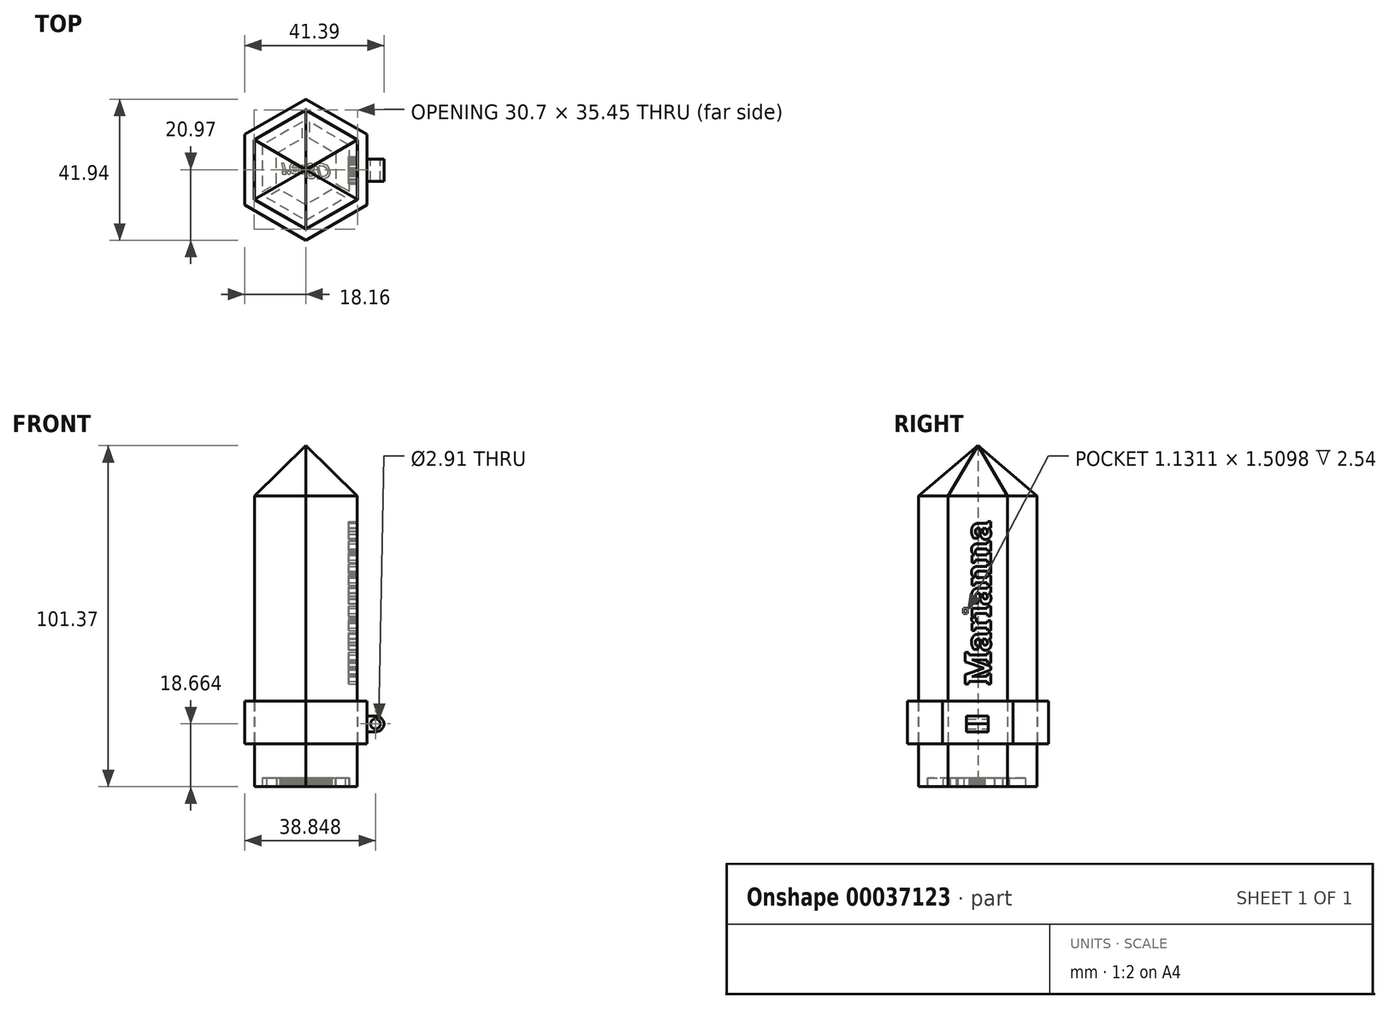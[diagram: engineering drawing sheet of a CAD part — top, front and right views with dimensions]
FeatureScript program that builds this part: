
annotation { "Feature Type Name" : "Feature", "Feature Type Description" : "" }
export const myFeature = defineFeature(function(context is Context, id is Id, definition is map)
    precondition{}
    {
        {
            var Q0;
            Q0=qCreatedBy(makeId("Top.planeOp"),FACE);
            var sketch = newSketch(context, id + "F0", { "sketchPlane" : qUnion([Q0])});
            skCircle(sketch, "E0.cCircle", {"center": v(0, 0) * mm, "radius": 15.24 * mm, "construction": true});
            skLineSegment(sketch, "E0.0", {"start": v(15.24, 8.8) * mm, "end": v(15.24, -8.8) * mm});
            skLineSegment(sketch, "E0.1", {"start": v(15.24, -8.8) * mm, "end": v(0, -17.6) * mm});
            skLineSegment(sketch, "E0.2", {"start": v(0, -17.6) * mm, "end": v(-15.24, -8.8) * mm});
            skLineSegment(sketch, "E0.3", {"start": v(-15.24, -8.8) * mm, "end": v(-15.24, 8.8) * mm});
            skLineSegment(sketch, "E0.4", {"start": v(-15.24, 8.8) * mm, "end": v(0, 17.6) * mm});
            skLineSegment(sketch, "E0.5", {"start": v(0, 17.6) * mm, "end": v(15.24, 8.8) * mm});
            skPoint(sketch, "E0.0.midPoint", {"position": v(15.24, 0) * mm});
            skLineSegment(sketch, "E1", {"start": v(0, 17.6) * mm, "end": v(0, -17.6) * mm});
            skLineSegment(sketch, "E2", {"start": v(-15.24, 8.8) * mm, "end": v(15.24, -8.8) * mm});
            skLineSegment(sketch, "E3", {"start": v(15.24, 8.8) * mm, "end": v(-15.24, -8.8) * mm});
            skSolve(sketch);
        }
        {
            var Q0;
            {var subQ3=sQuery(id+"F0.wireOp",EDGE,"E0.0");Q0=makeQuery(id+"F0.imprint","IMPRINT",FACE,{"disambiguationData":[TD([[makeQuery(id+"F0.imprint","IMPRINT",EDGE,{"derivedFrom":subQ3}),-1.0]])]});}
            extrude(context, id + "F1", {"entities" : qUnion([Q0]), "depth" : 101.6 * mm});
        }
        {
            var Q0;
            Q0=qCreatedBy(makeId("Front.planeOp"),FACE);
            var sketch = newSketch(context, id + "F2", { "sketchPlane" : qUnion([Q0])});
            skLineSegment(sketch, "E4", {"start": v(0, 101.37) * mm, "end": v(19.32, 82.36) * mm});
            skLineSegment(sketch, "E5", {"start": v(19.32, 82.36) * mm, "end": v(19.32, 105.1) * mm});
            skLineSegment(sketch, "E6", {"start": v(19.32, 105.1) * mm, "end": v(0, 105.1) * mm});
            skLineSegment(sketch, "E7", {"start": v(0, 105.1) * mm, "end": v(0, 101.37) * mm});
            skSolve(sketch);
        }
        {
            var Q0;
            Q0 = qSketchRegion(id + "F2", true);
            extrude(context, id + "F3", {"entities" : qUnion([Q0]), "operationType" : NewBodyOperationType.REMOVE, "endBound" : BoundingType.SYMMETRIC, "oppositeDirection" : true, "depth" : 50.8 * mm});
        }
        {
            var Q0;
            Q0=makeQuery(id+"F1.opExtrude","SWEPT_BODY",BODY,{"disambiguationData":[OSD([sQuery(id+"F0.wireOp",EDGE,"E0.0"),sQuery(id+"F0.wireOp",EDGE,"E2"),sQuery(id+"F0.wireOp",EDGE,"E3")])]});
            var Q1;
            Q1=makeQuery(id+"F1.opExtrude","SWEPT_EDGE",EDGE,{"disambiguationData":[OSD([sQuery(id+"F0.wireOp",EDGE,"E1"),sQuery(id+"F0.wireOp",EDGE,"E2"),sQuery(id+"F0.wireOp",EDGE,"E3")])]});
            circularPattern(context, id + "F4", {"entities" : qUnion([Q0]), "axis" : qUnion([Q1]), "angle" : 60 * degree, "instanceCount" : 6});
        }
        {
            var Q0;
            Q0=qCreatedBy(makeId("Top.planeOp"),FACE);
            var sketch = newSketch(context, id + "F5", { "sketchPlane" : qUnion([Q0])});
            skCircle(sketch, "E8.cCircle", {"center": v(0, 0) * mm, "radius": 18.16 * mm, "construction": true});
            skLineSegment(sketch, "E8.0", {"start": v(18.16, 10.49) * mm, "end": v(18.16, -10.49) * mm});
            skLineSegment(sketch, "E8.1", {"start": v(18.16, -10.49) * mm, "end": v(0, -20.97) * mm});
            skLineSegment(sketch, "E8.2", {"start": v(0, -20.97) * mm, "end": v(-18.16, -10.49) * mm});
            skLineSegment(sketch, "E8.3", {"start": v(-18.16, -10.49) * mm, "end": v(-18.16, 10.49) * mm});
            skLineSegment(sketch, "E8.4", {"start": v(-18.16, 10.49) * mm, "end": v(0, 20.97) * mm});
            skLineSegment(sketch, "E8.5", {"start": v(0, 20.97) * mm, "end": v(18.16, 10.49) * mm});
            skPoint(sketch, "E8.0.midPoint", {"position": v(18.16, 0) * mm});
            skCircle(sketch, "E9.cCircle", {"center": v(0, 0) * mm, "radius": 15.35 * mm, "construction": true});
            skLineSegment(sketch, "E9.0", {"start": v(15.35, 8.86) * mm, "end": v(15.35, -8.86) * mm});
            skLineSegment(sketch, "E9.1", {"start": v(15.35, -8.86) * mm, "end": v(0, -17.73) * mm});
            skLineSegment(sketch, "E9.2", {"start": v(0, -17.73) * mm, "end": v(-15.35, -8.86) * mm});
            skLineSegment(sketch, "E9.3", {"start": v(-15.35, -8.86) * mm, "end": v(-15.35, 8.86) * mm});
            skLineSegment(sketch, "E9.4", {"start": v(-15.35, 8.86) * mm, "end": v(0, 17.73) * mm});
            skLineSegment(sketch, "E9.5", {"start": v(0, 17.73) * mm, "end": v(15.35, 8.86) * mm});
            skPoint(sketch, "E9.0.midPoint", {"position": v(15.35, 0) * mm});
            skSolve(sketch);
        }
        {
            var Q0;
            Q0 = qSketchRegion(id + "F5", true);
            extrude(context, id + "F6", {"entities" : qUnion([Q0]), "depth" : 25.4 * mm});
        }
        {
            var Q0;
            Q0 = qSketchRegion(id + "F5", true);
            extrude(context, id + "F7", {"entities" : qUnion([Q0]), "operationType" : NewBodyOperationType.REMOVE, "depth" : 12.7 * mm});
        }
        {
            var Q0;
            Q0=makeQuery(id+"F6.opExtrude","SWEPT_FACE",FACE,{"disambiguationData":[OSD([sQuery(id+"F5.wireOp",EDGE,"E8.0")])]});
            var sketch = newSketch(context, id + "F8", { "sketchPlane" : qUnion([Q0])});
            skPoint(sketch, "E10.firstSnap0", {"position": v(-10.49, 19.05) * mm});
            skLineSegment(sketch, "E11.bottom", {"start": v(-3.45, 20.98) * mm, "end": v(3.13, 20.98) * mm});
            skLineSegment(sketch, "E11.top", {"start": v(-3.45, 16.34) * mm, "end": v(3.13, 16.34) * mm});
            skLineSegment(sketch, "E11.left", {"start": v(-3.45, 20.98) * mm, "end": v(-3.45, 16.34) * mm});
            skLineSegment(sketch, "E11.right", {"start": v(3.13, 20.98) * mm, "end": v(3.13, 16.34) * mm});
            skSolve(sketch);
        }
        {
            var Q0;
            Q0=makeQuery(id+"F8.imprint","IMPRINT",FACE,{"disambiguationData":[TD([[makeQuery(id+"F8.imprint","IMPRINT",EDGE,{"derivedFrom":sQuery(id+"F8.wireOp",EDGE,"E11.bottom")}),-1.0]])]});
            extrude(context, id + "F9", {"entities" : qUnion([Q0]), "operationType" : NewBodyOperationType.ADD, "depth" : 5.08 * mm});
        }
        {
            var Q0;
            Q0=makeQuery(id+"F9.opExtrude","SWEPT_FACE",FACE,{"disambiguationData":[OSD([sQuery(id+"F8.wireOp",EDGE,"E11.right")])]});
            var sketch = newSketch(context, id + "F10", { "sketchPlane" : qUnion([Q0])});
            skCircle(sketch, "E12", {"center": v(-20.69, 18.66) * mm, "radius": 1.46 * mm});
            skSolve(sketch);
        }
        {
            var Q0;
            Q0 = qSketchRegion(id + "F10", true);
            extrude(context, id + "F11", {"entities" : qUnion([Q0]), "operationType" : NewBodyOperationType.REMOVE, "endBound" : BoundingType.SYMMETRIC, "oppositeDirection" : true, "depth" : 25.4 * mm});
        }
        {
            var Q0;
            Q0=makeQuery(id+"F9.opExtrude","CAP_EDGE",EDGE,{"disambiguationData":[OSD([sQuery(id+"F8.wireOp",EDGE,"E11.bottom")])],"isStart":false});
            var Q1;
            Q1=makeQuery(id+"F9.opExtrude","CAP_EDGE",EDGE,{"disambiguationData":[OSD([sQuery(id+"F8.wireOp",EDGE,"E11.top")])],"isStart":false});
            fillet(context, id + "F12", {"entities" : qUnion([Q0, Q1]), "radius" : 2.54 * mm, "tangentPropagation" : true, "allowEdgeOverflow" : false});
        }
        {
            var Q0;
            Q0=makeQuery(id+"F4.opPattern","COPY",EDGE,{"derivedFrom":makeQuery(id+"F1.opExtrude","CAP_EDGE",EDGE,{"disambiguationData":[OSD([sQuery(id+"F0.wireOp",EDGE,"E0.0")])],"isStart":true}),"instanceName":"3"});
            cPlane(context, id + "F13", {"entities" : qUnion([Q0]), "cplaneType" : CPlaneType.LINE_ANGLE, "offset" : 152.4 * mm, "angle" : 180 * degree, "width" : 152.4 * mm, "height" : 152.4 * mm});
        }
        {
            var Q0;
            Q0=qCreatedBy(id+"F13.planeOp",FACE);
            var sketch = newSketch(context, id + "F14", { "sketchPlane" : qUnion([Q0])});
            skLineSegment(sketch, "E13", {"start": v(6.15, 1.61) * mm, "end": v(5.9, 1.8) * mm});
            skLineSegment(sketch, "E14", {"start": v(5.9, 1.8) * mm, "end": v(5.6, 1.94) * mm});
            skLineSegment(sketch, "E15", {"start": v(5.6, 1.94) * mm, "end": v(5.26, 2.03) * mm});
            skLineSegment(sketch, "E16", {"start": v(5.26, 2.03) * mm, "end": v(4.85, 2.05) * mm});
            skLineSegment(sketch, "E17", {"start": v(4.85, 2.05) * mm, "end": v(4.55, 2.05) * mm});
            skLineSegment(sketch, "E18", {"start": v(4.55, 2.05) * mm, "end": v(3.77, -1.27) * mm});
            skLineSegment(sketch, "E19", {"start": v(3.77, -1.27) * mm, "end": v(4.36, -1.27) * mm});
            skLineSegment(sketch, "E20", {"start": v(4.36, -1.27) * mm, "end": v(5.29, -1.13) * mm});
            skLineSegment(sketch, "E21", {"start": v(5.29, -1.13) * mm, "end": v(6, -0.67) * mm});
            skLineSegment(sketch, "E22", {"start": v(6, -0.67) * mm, "end": v(6.22, -0.39) * mm});
            skLineSegment(sketch, "E23", {"start": v(6.22, -0.39) * mm, "end": v(6.39, -0.07) * mm});
            skLineSegment(sketch, "E24", {"start": v(6.39, -0.07) * mm, "end": v(6.49, 0.28) * mm});
            skLineSegment(sketch, "E25", {"start": v(6.49, 0.28) * mm, "end": v(6.52, 0.65) * mm});
            skLineSegment(sketch, "E26", {"start": v(6.52, 0.65) * mm, "end": v(6.43, 1.18) * mm});
            skLineSegment(sketch, "E27", {"start": v(6.43, 1.18) * mm, "end": v(6.15, 1.61) * mm});
            skLineSegment(sketch, "E28", {"start": v(-2.68, 0.11) * mm, "end": v(-2.71, 0.3) * mm});
            skLineSegment(sketch, "E29", {"start": v(-2.71, 0.3) * mm, "end": v(-2.82, 0.45) * mm});
            skLineSegment(sketch, "E30", {"start": v(-2.82, 0.45) * mm, "end": v(-3, 0.55) * mm});
            skLineSegment(sketch, "E31", {"start": v(-3, 0.55) * mm, "end": v(-3.23, 0.58) * mm});
            skLineSegment(sketch, "E32", {"start": v(-3.23, 0.58) * mm, "end": v(-3.5, 0.53) * mm});
            skLineSegment(sketch, "E33", {"start": v(-3.5, 0.53) * mm, "end": v(-3.72, 0.4) * mm});
            skLineSegment(sketch, "E34", {"start": v(-3.72, 0.4) * mm, "end": v(-3.9, 0.18) * mm});
            skLineSegment(sketch, "E35", {"start": v(-3.9, 0.18) * mm, "end": v(-4.04, -0.1) * mm});
            skLineSegment(sketch, "E36", {"start": v(-4.04, -0.1) * mm, "end": v(-2.7, -0.1) * mm});
            skLineSegment(sketch, "E37", {"start": v(-2.7, -0.1) * mm, "end": v(-2.68, 0.11) * mm});
            skLineSegment(sketch, "E38", {"start": v(0, 17.6) * mm, "end": v(-15.24, 8.8) * mm});
            skLineSegment(sketch, "E39", {"start": v(-15.24, 8.8) * mm, "end": v(-15.24, -8.8) * mm});
            skLineSegment(sketch, "E40", {"start": v(-15.24, -8.8) * mm, "end": v(0, -17.6) * mm});
            skLineSegment(sketch, "E41", {"start": v(0, -17.6) * mm, "end": v(15.24, -8.8) * mm});
            skLineSegment(sketch, "E42", {"start": v(15.24, -8.8) * mm, "end": v(15.24, 8.8) * mm});
            skLineSegment(sketch, "E43", {"start": v(15.24, 8.8) * mm, "end": v(0, 17.6) * mm});
            skLineSegment(sketch, "E44", {"start": v(0, 15) * mm, "end": v(11.75, 8.22) * mm});
            skLineSegment(sketch, "E45", {"start": v(11.75, 8.22) * mm, "end": v(7.78, 5.93) * mm});
            skLineSegment(sketch, "E46", {"start": v(7.78, 5.93) * mm, "end": v(0.02, 10.41) * mm});
            skLineSegment(sketch, "E47", {"start": v(0.02, 10.41) * mm, "end": v(-7.75, 5.93) * mm});
            skLineSegment(sketch, "E48", {"start": v(-7.75, 5.93) * mm, "end": v(-11.73, 8.23) * mm});
            skLineSegment(sketch, "E49", {"start": v(-11.73, 8.23) * mm, "end": v(0, 15) * mm});
            skLineSegment(sketch, "E50", {"start": v(3.31, 1.95) * mm, "end": v(3.47, 2.64) * mm});
            skLineSegment(sketch, "E51", {"start": v(3.47, 2.64) * mm, "end": v(4.94, 2.64) * mm});
            skLineSegment(sketch, "E52", {"start": v(4.94, 2.64) * mm, "end": v(6, 2.46) * mm});
            skLineSegment(sketch, "E53", {"start": v(6, 2.46) * mm, "end": v(6.71, 2) * mm});
            skLineSegment(sketch, "E54", {"start": v(6.71, 2) * mm, "end": v(6.93, 1.73) * mm});
            skLineSegment(sketch, "E55", {"start": v(6.93, 1.73) * mm, "end": v(7.1, 1.4) * mm});
            skLineSegment(sketch, "E56", {"start": v(7.1, 1.4) * mm, "end": v(7.18, 1.05) * mm});
            skLineSegment(sketch, "E57", {"start": v(7.18, 1.05) * mm, "end": v(7.22, 0.68) * mm});
            skLineSegment(sketch, "E58", {"start": v(7.22, 0.68) * mm, "end": v(7.04, -0.28) * mm});
            skLineSegment(sketch, "E59", {"start": v(7.04, -0.28) * mm, "end": v(6.5, -1.05) * mm});
            skLineSegment(sketch, "E60", {"start": v(6.5, -1.05) * mm, "end": v(6.04, -1.42) * mm});
            skLineSegment(sketch, "E61", {"start": v(6.04, -1.42) * mm, "end": v(5.5, -1.66) * mm});
            skLineSegment(sketch, "E62", {"start": v(5.5, -1.66) * mm, "end": v(4.9, -1.8) * mm});
            skLineSegment(sketch, "E63", {"start": v(4.9, -1.8) * mm, "end": v(4.25, -1.85) * mm});
            skLineSegment(sketch, "E64", {"start": v(4.25, -1.85) * mm, "end": v(2.5, -1.85) * mm});
            skLineSegment(sketch, "E65", {"start": v(2.5, -1.85) * mm, "end": v(2.66, -1.16) * mm});
            skLineSegment(sketch, "E66", {"start": v(2.66, -1.16) * mm, "end": v(3.13, -1.16) * mm});
            skLineSegment(sketch, "E67", {"start": v(3.13, -1.16) * mm, "end": v(3.86, 1.95) * mm});
            skLineSegment(sketch, "E68", {"start": v(3.86, 1.95) * mm, "end": v(3.31, 1.95) * mm});
            skLineSegment(sketch, "E69", {"start": v(-7.17, 0.62) * mm, "end": v(-7, 1.25) * mm});
            skLineSegment(sketch, "E70", {"start": v(-7, 1.25) * mm, "end": v(-5.84, 1.25) * mm});
            skLineSegment(sketch, "E71", {"start": v(-5.84, 1.25) * mm, "end": v(-6.03, 0.37) * mm});
            skLineSegment(sketch, "E72", {"start": v(-6.03, 0.37) * mm, "end": v(-5.77, 0.79) * mm});
            skLineSegment(sketch, "E73", {"start": v(-5.77, 0.79) * mm, "end": v(-5.5, 1.08) * mm});
            skLineSegment(sketch, "E74", {"start": v(-5.5, 1.08) * mm, "end": v(-5.24, 1.25) * mm});
            skLineSegment(sketch, "E75", {"start": v(-5.24, 1.25) * mm, "end": v(-4.97, 1.3) * mm});
            skLineSegment(sketch, "E76", {"start": v(-4.97, 1.3) * mm, "end": v(-4.79, 1.27) * mm});
            skLineSegment(sketch, "E77", {"start": v(-4.79, 1.27) * mm, "end": v(-4.63, 1.17) * mm});
            skLineSegment(sketch, "E78", {"start": v(-4.63, 1.17) * mm, "end": v(-4.52, 1.01) * mm});
            skLineSegment(sketch, "E79", {"start": v(-4.52, 1.01) * mm, "end": v(-4.47, 0.81) * mm});
            skLineSegment(sketch, "E80", {"start": v(-4.47, 0.81) * mm, "end": v(-4.5, 0.63) * mm});
            skLineSegment(sketch, "E81", {"start": v(-4.5, 0.63) * mm, "end": v(-4.61, 0.48) * mm});
            skLineSegment(sketch, "E82", {"start": v(-4.61, 0.48) * mm, "end": v(-4.76, 0.38) * mm});
            skLineSegment(sketch, "E83", {"start": v(-4.76, 0.38) * mm, "end": v(-4.94, 0.34) * mm});
            skLineSegment(sketch, "E84", {"start": v(-4.94, 0.34) * mm, "end": v(-5.11, 0.37) * mm});
            skLineSegment(sketch, "E85", {"start": v(-5.11, 0.37) * mm, "end": v(-5.25, 0.45) * mm});
            skLineSegment(sketch, "E86", {"start": v(-5.25, 0.45) * mm, "end": v(-5.34, 0.56) * mm});
            skLineSegment(sketch, "E87", {"start": v(-5.34, 0.56) * mm, "end": v(-5.4, 0.68) * mm});
            skLineSegment(sketch, "E88", {"start": v(-5.4, 0.68) * mm, "end": v(-5.58, 0.57) * mm});
            skLineSegment(sketch, "E89", {"start": v(-5.58, 0.57) * mm, "end": v(-5.78, 0.35) * mm});
            skLineSegment(sketch, "E90", {"start": v(-5.78, 0.35) * mm, "end": v(-5.97, 0.03) * mm});
            skLineSegment(sketch, "E91", {"start": v(-5.97, 0.03) * mm, "end": v(-6.11, -0.38) * mm});
            skLineSegment(sketch, "E92", {"start": v(-6.11, -0.38) * mm, "end": v(-6.45, -1.89) * mm});
            skLineSegment(sketch, "E93", {"start": v(-6.45, -1.89) * mm, "end": v(-7.22, -1.89) * mm});
            skLineSegment(sketch, "E94", {"start": v(-7.22, -1.89) * mm, "end": v(-6.62, 0.62) * mm});
            skLineSegment(sketch, "E95", {"start": v(-6.62, 0.62) * mm, "end": v(-7.17, 0.62) * mm});
            skLineSegment(sketch, "E96", {"start": v(-7.17, 0.62) * mm, "end": v(-7.17, 0.62) * mm});
            skLineSegment(sketch, "E97", {"start": v(-1.06, -14.18) * mm, "end": v(-12.9, -7.34) * mm});
            skLineSegment(sketch, "E98", {"start": v(-12.9, -7.34) * mm, "end": v(-12.9, 6.46) * mm});
            skLineSegment(sketch, "E99", {"start": v(-12.9, 6.46) * mm, "end": v(-8.8, 4.1) * mm});
            skLineSegment(sketch, "E100", {"start": v(-8.8, 4.1) * mm, "end": v(-8.8, -4.87) * mm});
            skLineSegment(sketch, "E101", {"start": v(-8.8, -4.87) * mm, "end": v(-1.06, -9.34) * mm});
            skLineSegment(sketch, "E102", {"start": v(-1.06, -9.34) * mm, "end": v(-1.06, -14.18) * mm});
            skLineSegment(sketch, "E103", {"start": v(-1.02, -1.29) * mm, "end": v(-1.25, -1.24) * mm});
            skLineSegment(sketch, "E104", {"start": v(-1.25, -1.24) * mm, "end": v(-1.42, -1.1) * mm});
            skLineSegment(sketch, "E105", {"start": v(-1.42, -1.1) * mm, "end": v(-1.8, -1.28) * mm});
            skLineSegment(sketch, "E106", {"start": v(-1.8, -1.28) * mm, "end": v(-2.2, -1.6) * mm});
            skLineSegment(sketch, "E107", {"start": v(-2.2, -1.6) * mm, "end": v(-2.73, -1.89) * mm});
            skLineSegment(sketch, "E108", {"start": v(-2.73, -1.89) * mm, "end": v(-3.48, -2.02) * mm});
            skLineSegment(sketch, "E109", {"start": v(-3.48, -2.02) * mm, "end": v(-3.7, -2) * mm});
            skLineSegment(sketch, "E110", {"start": v(-3.7, -2) * mm, "end": v(-3.93, -1.92) * mm});
            skLineSegment(sketch, "E111", {"start": v(-3.93, -1.92) * mm, "end": v(-4.17, -1.8) * mm});
            skLineSegment(sketch, "E112", {"start": v(-4.17, -1.8) * mm, "end": v(-4.38, -1.63) * mm});
            skLineSegment(sketch, "E113", {"start": v(-4.38, -1.63) * mm, "end": v(-4.57, -1.43) * mm});
            skLineSegment(sketch, "E114", {"start": v(-4.57, -1.43) * mm, "end": v(-4.73, -1.2) * mm});
            skLineSegment(sketch, "E115", {"start": v(-4.73, -1.2) * mm, "end": v(-4.82, -0.92) * mm});
            skLineSegment(sketch, "E116", {"start": v(-4.82, -0.92) * mm, "end": v(-4.86, -0.62) * mm});
            skLineSegment(sketch, "E117", {"start": v(-4.86, -0.62) * mm, "end": v(-4.73, 0.09) * mm});
            skLineSegment(sketch, "E118", {"start": v(-4.73, 0.09) * mm, "end": v(-4.39, 0.66) * mm});
            skLineSegment(sketch, "E119", {"start": v(-4.39, 0.66) * mm, "end": v(-3.87, 1.05) * mm});
            skLineSegment(sketch, "E120", {"start": v(-3.87, 1.05) * mm, "end": v(-3.24, 1.2) * mm});
            skLineSegment(sketch, "E121", {"start": v(-3.24, 1.2) * mm, "end": v(-2.72, 1.12) * mm});
            skLineSegment(sketch, "E122", {"start": v(-2.72, 1.12) * mm, "end": v(-2.32, 0.9) * mm});
            skLineSegment(sketch, "E123", {"start": v(-2.32, 0.9) * mm, "end": v(-2.05, 0.53) * mm});
            skLineSegment(sketch, "E124", {"start": v(-2.05, 0.53) * mm, "end": v(-1.96, 0.04) * mm});
            skLineSegment(sketch, "E125", {"start": v(-1.96, 0.04) * mm, "end": v(-1.99, -0.27) * mm});
            skLineSegment(sketch, "E126", {"start": v(-1.99, -0.27) * mm, "end": v(-2.07, -0.61) * mm});
            skLineSegment(sketch, "E127", {"start": v(-2.07, -0.61) * mm, "end": v(-4.12, -0.61) * mm});
            skLineSegment(sketch, "E128", {"start": v(-4.12, -0.61) * mm, "end": v(-4.12, -0.66) * mm});
            skLineSegment(sketch, "E129", {"start": v(-4.12, -0.66) * mm, "end": v(-4.07, -0.91) * mm});
            skLineSegment(sketch, "E130", {"start": v(-4.07, -0.91) * mm, "end": v(-3.9, -1.15) * mm});
            skLineSegment(sketch, "E131", {"start": v(-3.9, -1.15) * mm, "end": v(-3.63, -1.32) * mm});
            skLineSegment(sketch, "E132", {"start": v(-3.63, -1.32) * mm, "end": v(-3.26, -1.4) * mm});
            skLineSegment(sketch, "E133", {"start": v(-3.26, -1.4) * mm, "end": v(-2.72, -1.29) * mm});
            skLineSegment(sketch, "E134", {"start": v(-2.72, -1.29) * mm, "end": v(-2.2, -1.01) * mm});
            skLineSegment(sketch, "E135", {"start": v(-2.2, -1.01) * mm, "end": v(-1.76, -0.68) * mm});
            skLineSegment(sketch, "E136", {"start": v(-1.76, -0.68) * mm, "end": v(-1.43, -0.4) * mm});
            skLineSegment(sketch, "E137", {"start": v(-1.43, -0.4) * mm, "end": v(-1.3, -0.3) * mm});
            skLineSegment(sketch, "E138", {"start": v(-1.3, -0.3) * mm, "end": v(-1.24, -0.28) * mm});
            skLineSegment(sketch, "E139", {"start": v(-1.24, -0.28) * mm, "end": v(-1.22, -0.28) * mm});
            skLineSegment(sketch, "E140", {"start": v(-1.22, -0.28) * mm, "end": v(-1.02, -0.24) * mm});
            skLineSegment(sketch, "E141", {"start": v(-1.02, -0.24) * mm, "end": v(-0.82, -0.28) * mm});
            skLineSegment(sketch, "E142", {"start": v(-0.82, -0.28) * mm, "end": v(-0.65, -0.4) * mm});
            skLineSegment(sketch, "E143", {"start": v(-0.65, -0.4) * mm, "end": v(-0.54, -0.56) * mm});
            skLineSegment(sketch, "E144", {"start": v(-0.54, -0.56) * mm, "end": v(-0.5, -0.76) * mm});
            skLineSegment(sketch, "E145", {"start": v(-0.5, -0.76) * mm, "end": v(-0.54, -0.97) * mm});
            skLineSegment(sketch, "E146", {"start": v(-0.54, -0.97) * mm, "end": v(-0.65, -1.13) * mm});
            skLineSegment(sketch, "E147", {"start": v(-0.65, -1.13) * mm, "end": v(-0.82, -1.25) * mm});
            skLineSegment(sketch, "E148", {"start": v(-0.82, -1.25) * mm, "end": v(-1.02, -1.29) * mm});
            skLineSegment(sketch, "E149", {"start": v(-0.67, 0.24) * mm, "end": v(-0.7, 0.22) * mm});
            skLineSegment(sketch, "E150", {"start": v(-0.7, 0.22) * mm, "end": v(-0.77, 0.19) * mm});
            skLineSegment(sketch, "E151", {"start": v(-0.77, 0.19) * mm, "end": v(-1.01, 0.13) * mm});
            skLineSegment(sketch, "E152", {"start": v(-1.01, 0.13) * mm, "end": v(-1.22, 0.17) * mm});
            skLineSegment(sketch, "E153", {"start": v(-1.22, 0.17) * mm, "end": v(-1.4, 0.29) * mm});
            skLineSegment(sketch, "E154", {"start": v(-1.4, 0.29) * mm, "end": v(-1.51, 0.46) * mm});
            skLineSegment(sketch, "E155", {"start": v(-1.51, 0.46) * mm, "end": v(-1.55, 0.67) * mm});
            skLineSegment(sketch, "E156", {"start": v(-1.55, 0.67) * mm, "end": v(-1.51, 0.88) * mm});
            skLineSegment(sketch, "E157", {"start": v(-1.51, 0.88) * mm, "end": v(-1.4, 1.05) * mm});
            skLineSegment(sketch, "E158", {"start": v(-1.4, 1.05) * mm, "end": v(-1.23, 1.17) * mm});
            skLineSegment(sketch, "E159", {"start": v(-1.23, 1.17) * mm, "end": v(-1.02, 1.2) * mm});
            skLineSegment(sketch, "E160", {"start": v(-1.02, 1.2) * mm, "end": v(-1.01, 1.21) * mm});
            skLineSegment(sketch, "E161", {"start": v(-1.01, 1.21) * mm, "end": v(-1, 1.21) * mm});
            skLineSegment(sketch, "E162", {"start": v(-1, 1.21) * mm, "end": v(-0.97, 1.2) * mm});
            skLineSegment(sketch, "E163", {"start": v(-0.97, 1.2) * mm, "end": v(-0.96, 1.2) * mm});
            skLineSegment(sketch, "E164", {"start": v(-0.96, 1.2) * mm, "end": v(-0.95, 1.2) * mm});
            skLineSegment(sketch, "E165", {"start": v(-0.95, 1.2) * mm, "end": v(-0.94, 1.2) * mm});
            skLineSegment(sketch, "E166", {"start": v(-0.94, 1.2) * mm, "end": v(-0.78, 1.16) * mm});
            skLineSegment(sketch, "E167", {"start": v(-0.78, 1.16) * mm, "end": v(-0.46, 0.95) * mm});
            skLineSegment(sketch, "E168", {"start": v(-0.46, 0.95) * mm, "end": v(-0.2, 0.62) * mm});
            skLineSegment(sketch, "E169", {"start": v(-0.2, 0.62) * mm, "end": v(0.02, 0.21) * mm});
            skLineSegment(sketch, "E170", {"start": v(0.02, 0.21) * mm, "end": v(0.22, -0.21) * mm});
            skLineSegment(sketch, "E171", {"start": v(0.22, -0.21) * mm, "end": v(0.41, -0.62) * mm});
            skLineSegment(sketch, "E172", {"start": v(0.41, -0.62) * mm, "end": v(0.63, -0.96) * mm});
            skLineSegment(sketch, "E173", {"start": v(0.63, -0.96) * mm, "end": v(0.87, -1.2) * mm});
            skLineSegment(sketch, "E174", {"start": v(0.87, -1.2) * mm, "end": v(1.17, -1.27) * mm});
            skLineSegment(sketch, "E175", {"start": v(1.17, -1.27) * mm, "end": v(1.5, -1.2) * mm});
            skLineSegment(sketch, "E176", {"start": v(1.5, -1.2) * mm, "end": v(1.7, -1.04) * mm});
            skLineSegment(sketch, "E177", {"start": v(1.7, -1.04) * mm, "end": v(1.82, -0.81) * mm});
            skLineSegment(sketch, "E178", {"start": v(1.82, -0.81) * mm, "end": v(1.85, -0.55) * mm});
            skLineSegment(sketch, "E179", {"start": v(1.85, -0.55) * mm, "end": v(1.79, -0.27) * mm});
            skLineSegment(sketch, "E180", {"start": v(1.79, -0.27) * mm, "end": v(1.61, -0.04) * mm});
            skLineSegment(sketch, "E181", {"start": v(1.61, -0.04) * mm, "end": v(1.33, 0.1) * mm});
            skLineSegment(sketch, "E182", {"start": v(1.33, 0.1) * mm, "end": v(0.93, 0.16) * mm});
            skLineSegment(sketch, "E183", {"start": v(0.93, 0.16) * mm, "end": v(0.73, 0.16) * mm});
            skLineSegment(sketch, "E184", {"start": v(0.73, 0.16) * mm, "end": v(0.88, 0.74) * mm});
            skLineSegment(sketch, "E185", {"start": v(0.88, 0.74) * mm, "end": v(1.05, 0.74) * mm});
            skLineSegment(sketch, "E186", {"start": v(1.05, 0.74) * mm, "end": v(1.5, 0.8) * mm});
            skLineSegment(sketch, "E187", {"start": v(1.5, 0.8) * mm, "end": v(1.87, 0.93) * mm});
            skLineSegment(sketch, "E188", {"start": v(1.87, 0.93) * mm, "end": v(2.12, 1.16) * mm});
            skLineSegment(sketch, "E189", {"start": v(2.12, 1.16) * mm, "end": v(2.22, 1.47) * mm});
            skLineSegment(sketch, "E190", {"start": v(2.22, 1.47) * mm, "end": v(2.16, 1.7) * mm});
            skLineSegment(sketch, "E191", {"start": v(2.16, 1.7) * mm, "end": v(2.01, 1.86) * mm});
            skLineSegment(sketch, "E192", {"start": v(2.01, 1.86) * mm, "end": v(1.8, 1.96) * mm});
            skLineSegment(sketch, "E193", {"start": v(1.8, 1.96) * mm, "end": v(1.5, 2) * mm});
            skLineSegment(sketch, "E194", {"start": v(1.5, 2) * mm, "end": v(1.14, 1.96) * mm});
            skLineSegment(sketch, "E195", {"start": v(1.14, 1.96) * mm, "end": v(0.96, 1.88) * mm});
            skLineSegment(sketch, "E196", {"start": v(0.96, 1.88) * mm, "end": v(1.03, 1.64) * mm});
            skLineSegment(sketch, "E197", {"start": v(1.03, 1.64) * mm, "end": v(1, 1.47) * mm});
            skLineSegment(sketch, "E198", {"start": v(1, 1.47) * mm, "end": v(0.91, 1.34) * mm});
            skLineSegment(sketch, "E199", {"start": v(0.91, 1.34) * mm, "end": v(0.78, 1.25) * mm});
            skLineSegment(sketch, "E200", {"start": v(0.78, 1.25) * mm, "end": v(0.61, 1.21) * mm});
            skLineSegment(sketch, "E201", {"start": v(0.61, 1.21) * mm, "end": v(0.46, 1.24) * mm});
            skLineSegment(sketch, "E202", {"start": v(0.46, 1.24) * mm, "end": v(0.32, 1.32) * mm});
            skLineSegment(sketch, "E203", {"start": v(0.32, 1.32) * mm, "end": v(0.21, 1.46) * mm});
            skLineSegment(sketch, "E204", {"start": v(0.21, 1.46) * mm, "end": v(0.17, 1.68) * mm});
            skLineSegment(sketch, "E205", {"start": v(0.17, 1.68) * mm, "end": v(0.27, 2.03) * mm});
            skLineSegment(sketch, "E206", {"start": v(0.27, 2.03) * mm, "end": v(0.55, 2.33) * mm});
            skLineSegment(sketch, "E207", {"start": v(0.55, 2.33) * mm, "end": v(0.98, 2.54) * mm});
            skLineSegment(sketch, "E208", {"start": v(0.98, 2.54) * mm, "end": v(1.55, 2.61) * mm});
            skLineSegment(sketch, "E209", {"start": v(1.55, 2.61) * mm, "end": v(2.13, 2.53) * mm});
            skLineSegment(sketch, "E210", {"start": v(2.13, 2.53) * mm, "end": v(2.58, 2.3) * mm});
            skLineSegment(sketch, "E211", {"start": v(2.58, 2.3) * mm, "end": v(2.87, 1.95) * mm});
            skLineSegment(sketch, "E212", {"start": v(2.87, 1.95) * mm, "end": v(2.98, 1.5) * mm});
            skLineSegment(sketch, "E213", {"start": v(2.98, 1.5) * mm, "end": v(2.91, 1.15) * mm});
            skLineSegment(sketch, "E214", {"start": v(2.91, 1.15) * mm, "end": v(2.7, 0.83) * mm});
            skLineSegment(sketch, "E215", {"start": v(2.7, 0.83) * mm, "end": v(2.34, 0.57) * mm});
            skLineSegment(sketch, "E216", {"start": v(2.34, 0.57) * mm, "end": v(1.8, 0.42) * mm});
            skLineSegment(sketch, "E217", {"start": v(1.8, 0.42) * mm, "end": v(2.16, 0.22) * mm});
            skLineSegment(sketch, "E218", {"start": v(2.16, 0.22) * mm, "end": v(2.41, -0.03) * mm});
            skLineSegment(sketch, "E219", {"start": v(2.41, -0.03) * mm, "end": v(2.55, -0.3) * mm});
            skLineSegment(sketch, "E220", {"start": v(2.55, -0.3) * mm, "end": v(2.6, -0.6) * mm});
            skLineSegment(sketch, "E221", {"start": v(2.6, -0.6) * mm, "end": v(2.58, -0.86) * mm});
            skLineSegment(sketch, "E222", {"start": v(2.58, -0.86) * mm, "end": v(2.52, -1.1) * mm});
            skLineSegment(sketch, "E223", {"start": v(2.52, -1.1) * mm, "end": v(2.42, -1.32) * mm});
            skLineSegment(sketch, "E224", {"start": v(2.42, -1.32) * mm, "end": v(2.28, -1.52) * mm});
            skLineSegment(sketch, "E225", {"start": v(2.28, -1.52) * mm, "end": v(2.1, -1.68) * mm});
            skLineSegment(sketch, "E226", {"start": v(2.1, -1.68) * mm, "end": v(1.86, -1.8) * mm});
            skLineSegment(sketch, "E227", {"start": v(1.86, -1.8) * mm, "end": v(1.58, -1.87) * mm});
            skLineSegment(sketch, "E228", {"start": v(1.58, -1.87) * mm, "end": v(1.24, -1.9) * mm});
            skLineSegment(sketch, "E229", {"start": v(1.24, -1.9) * mm, "end": v(0.72, -1.8) * mm});
            skLineSegment(sketch, "E230", {"start": v(0.72, -1.8) * mm, "end": v(0.35, -1.56) * mm});
            skLineSegment(sketch, "E231", {"start": v(0.35, -1.56) * mm, "end": v(0.09, -1.23) * mm});
            skLineSegment(sketch, "E232", {"start": v(0.09, -1.23) * mm, "end": v(-0.1, -0.86) * mm});
            skLineSegment(sketch, "E233", {"start": v(-0.1, -0.86) * mm, "end": v(-0.23, -0.48) * mm});
            skLineSegment(sketch, "E234", {"start": v(-0.23, -0.48) * mm, "end": v(-0.35, -0.14) * mm});
            skLineSegment(sketch, "E235", {"start": v(-0.35, -0.14) * mm, "end": v(-0.49, 0.1) * mm});
            skLineSegment(sketch, "E236", {"start": v(-0.49, 0.1) * mm, "end": v(-0.67, 0.24) * mm});
            skLineSegment(sketch, "E237", {"start": v(12.9, -7.34) * mm, "end": v(1.06, -14.18) * mm});
            skLineSegment(sketch, "E238", {"start": v(1.06, -14.18) * mm, "end": v(1.06, -9.36) * mm});
            skLineSegment(sketch, "E239", {"start": v(1.06, -9.36) * mm, "end": v(8.84, -4.87) * mm});
            skLineSegment(sketch, "E240", {"start": v(8.84, -4.87) * mm, "end": v(8.84, 4.1) * mm});
            skLineSegment(sketch, "E241", {"start": v(8.84, 4.1) * mm, "end": v(10.3, 4.93) * mm});
            skLineSegment(sketch, "E242", {"start": v(10.3, 4.93) * mm, "end": v(12.9, 6.44) * mm});
            skLineSegment(sketch, "E243", {"start": v(12.9, 6.44) * mm, "end": v(12.9, -7.34) * mm});
            skSolve(sketch);
        }
        {
            var Q0;
            Q0=makeQuery(id+"F14.imprint","IMPRINT",FACE,{"disambiguationData":[TD([[makeQuery(id+"F14.imprint","IMPRINT",EDGE,{"derivedFrom":sQuery(id+"F14.wireOp",EDGE,"E237")}),-1.0]])]});
            var Q1;
            Q1=makeQuery(id+"F14.imprint","IMPRINT",FACE,{"disambiguationData":[TD([[makeQuery(id+"F14.imprint","IMPRINT",EDGE,{"derivedFrom":sQuery(id+"F14.wireOp",EDGE,"E44")}),-1.0]])]});
            var Q2;
            Q2=makeQuery(id+"F14.imprint","IMPRINT",FACE,{"disambiguationData":[TD([[makeQuery(id+"F14.imprint","IMPRINT",EDGE,{"derivedFrom":sQuery(id+"F14.wireOp",EDGE,"E97")}),-1.0]])]});
            extrude(context, id + "F15", {"entities" : qUnion([Q0, Q1, Q2]), "operationType" : NewBodyOperationType.REMOVE, "oppositeDirection" : true, "depth" : 2.54 * mm});
        }
        {
            var Q0;
            {var subQ4=sQuery(id+"F14.wireOp",EDGE,"E70");Q0=makeQuery(id+"F14.imprint","IMPRINT",FACE,{"disambiguationData":[TD([[makeQuery(id+"F14.imprint","IMPRINT",EDGE,{"derivedFrom":subQ4}),-1.0]])]});}
            var Q1;
            Q1=makeQuery(id+"F14.imprint","IMPRINT",FACE,{"disambiguationData":[TD([[makeQuery(id+"F14.imprint","IMPRINT",EDGE,{"derivedFrom":sQuery(id+"F14.wireOp",EDGE,"E28")}),-1.0]])]});
            var Q2;
            Q2=makeQuery(id+"F14.imprint","IMPRINT",FACE,{"disambiguationData":[TD([[makeQuery(id+"F14.imprint","IMPRINT",EDGE,{"derivedFrom":sQuery(id+"F14.wireOp",EDGE,"E149")}),-1.0]])]});
            var Q3;
            Q3=makeQuery(id+"F14.imprint","IMPRINT",FACE,{"disambiguationData":[TD([[makeQuery(id+"F14.imprint","IMPRINT",EDGE,{"derivedFrom":sQuery(id+"F14.wireOp",EDGE,"E13")}),-1.0]])]});
            extrude(context, id + "F16", {"entities" : qUnion([Q0, Q1, Q2, Q3]), "operationType" : NewBodyOperationType.REMOVE, "oppositeDirection" : true, "depth" : 2.54 * mm});
        }
        {
            var Q0;
            Q0=makeQuery(id+"F1.opExtrude","SWEPT_FACE",FACE,{"disambiguationData":[OSD([sQuery(id+"F0.wireOp",EDGE,"E0.0")])]});
            var sketch = newSketch(context, id + "F17", { "sketchPlane" : qUnion([Q0])});
            skText(sketch, "E244", { "text": "Marianna", "fontName": "RobotoSlab-Bold.ttf"});
            const initialGuessF17  = {"E244": [0.00381, 0.03021, 0, 1, 0.00762]};
            skSetInitialGuess(sketch, initialGuessF17);
            skSolve(sketch);
        }
        {
            var Q0;
            Q0 = qSketchRegion(id + "F17", true);
            extrude(context, id + "F18", {"entities" : qUnion([Q0]), "operationType" : NewBodyOperationType.REMOVE, "oppositeDirection" : true, "depth" : 2.54 * mm});
        }
    });
